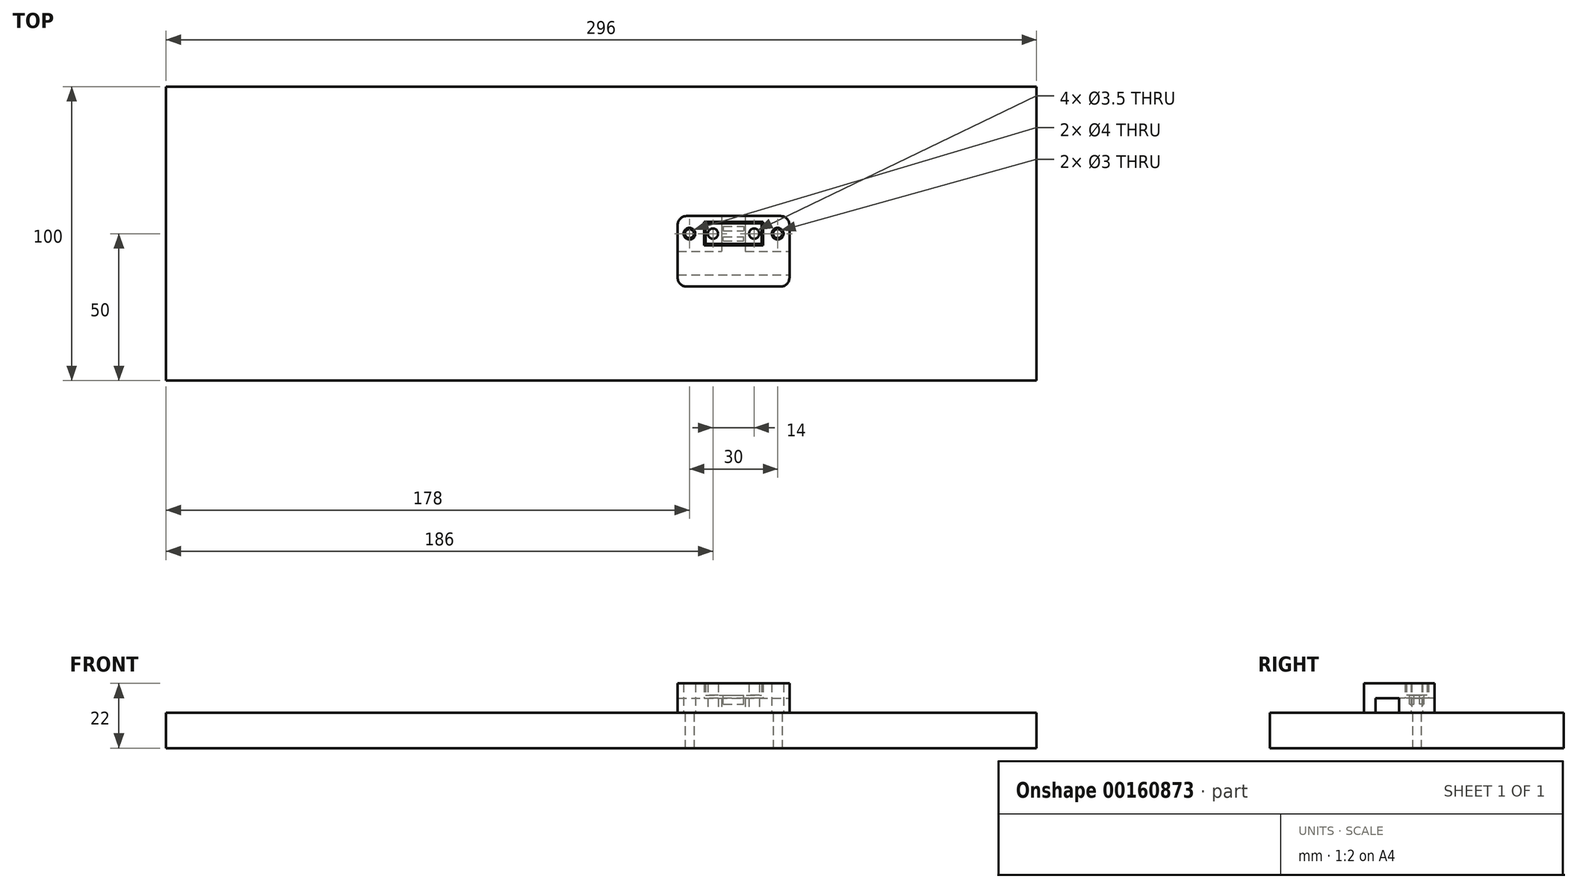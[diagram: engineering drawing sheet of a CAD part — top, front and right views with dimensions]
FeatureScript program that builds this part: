
annotation { "Feature Type Name" : "Feature", "Feature Type Description" : "" }
export const myFeature = defineFeature(function(context is Context, id is Id, definition is map)
    precondition{}
    {
        {
            var Q0;
            Q0=qCreatedBy(makeId("Top.planeOp"),FACE);
            var sketch = newSketch(context, id + "F0", { "sketchPlane" : qUnion([Q0])});
            skLineSegment(sketch, "E0.bottom", {"start": v(-148, 50) * mm, "end": v(148, 50) * mm});
            skLineSegment(sketch, "E0.top", {"start": v(-148, -50) * mm, "end": v(148, -50) * mm});
            skLineSegment(sketch, "E0.left", {"start": v(-148, 50) * mm, "end": v(-148, -50) * mm});
            skLineSegment(sketch, "E0.right", {"start": v(148, 50) * mm, "end": v(148, -50) * mm});
            skPoint(sketch, "E1", {"position": v(0, 50) * mm});
            skPoint(sketch, "E2", {"position": v(148, 0) * mm});
            skCircle(sketch, "E3", {"center": v(60, 0) * mm, "radius": 1.5 * mm});
            skCircle(sketch, "E4.MirrorC", {"center": v(30, 0) * mm, "radius": 1.5 * mm});
            skSolve(sketch);
        }
        {
            var Q0;
            Q0 = qSketchRegion(id + "F0", true);
            extrude(context, id + "F1", {"entities" : qUnion([Q0]), "depth" : 12 * mm});
        }
        {
            var Q0;
            Q0=makeQuery(id+"F1.opExtrude","CAP_FACE",FACE,{"disambiguationData":[OSD([sQuery(id+"F0.wireOp",EDGE,"E0.bottom"),sQuery(id+"F0.wireOp",EDGE,"E0.top"),sQuery(id+"F0.wireOp",EDGE,"E0.left"),sQuery(id+"F0.wireOp",EDGE,"E0.right"),sQuery(id+"F0.wireOp",EDGE,"E3"),sQuery(id+"F0.wireOp",EDGE,"E4.MirrorC")])],"isStart":false});
            var sketch = newSketch(context, id + "F2", { "sketchPlane" : qUnion([Q0])});
            skLineSegment(sketch, "E5", {"start": v(30, 0) * mm, "end": v(60, 0) * mm, "construction": true});
            skLineSegment(sketch, "E6", {"start": v(45, 0) * mm, "end": v(45, 6) * mm, "construction": true});
            skLineSegment(sketch, "E7", {"start": v(29, 6) * mm, "end": v(41, 6) * mm});
            skLineSegment(sketch, "E8.MirrorCS", {"start": v(29, -18) * mm, "end": v(61, -18) * mm});
            skArc(sketch, "E9", {"start": v(64, 3) * mm, "mid": v(63.12, 5.12) * mm, "end": v(61, 6) * mm});
            skArc(sketch, "E10.MirrorCS", {"start": v(26, 3) * mm, "mid": v(26.88, 5.12) * mm, "end": v(29, 6) * mm});
            skArc(sketch, "E11", {"start": v(61, -18) * mm, "mid": v(63.12, -17.12) * mm, "end": v(64, -15) * mm});
            skLineSegment(sketch, "E12", {"start": v(64, -15) * mm, "end": v(64, -14) * mm});
            skArc(sketch, "E13.MirrorCS", {"start": v(29, -18) * mm, "mid": v(26.88, -17.12) * mm, "end": v(26, -15) * mm});
            skLineSegment(sketch, "E14.MirrorCS", {"start": v(26, -15) * mm, "end": v(26, -14) * mm});
            skLineSegment(sketch, "E15", {"start": v(26, -14) * mm, "end": v(64, -14) * mm});
            skLineSegment(sketch, "E16", {"start": v(26, -6) * mm, "end": v(41, -6) * mm});
            skLineSegment(sketch, "E17.trimOffspring", {"start": v(26, -6) * mm, "end": v(26, 3) * mm});
            skLineSegment(sketch, "E18.trimOffspring", {"start": v(64, -6) * mm, "end": v(64, 3) * mm});
            skLineSegment(sketch, "E19", {"start": v(41, 6) * mm, "end": v(41, -6) * mm});
            skLineSegment(sketch, "E20.MirrorCS", {"start": v(49, 6) * mm, "end": v(49, -6) * mm});
            skLineSegment(sketch, "E21.trimOffspring", {"start": v(49, 6) * mm, "end": v(61, 6) * mm});
            skLineSegment(sketch, "E22.trimOffspring", {"start": v(49, -6) * mm, "end": v(64, -6) * mm});
            skCircle(sketch, "E23", {"center": v(60, 0) * mm, "radius": 2 * mm});
            skCircle(sketch, "E24.MirrorC", {"center": v(30, 0) * mm, "radius": 2 * mm});
            skCircle(sketch, "E25", {"center": v(38, 0) * mm, "radius": 1.75 * mm});
            skCircle(sketch, "E26.MirrorC", {"center": v(52, 0) * mm, "radius": 1.75 * mm});
            skSolve(sketch);
        }
        {
            var Q0;
            Q0 = qSketchRegion(id + "F2", true);
            extrude(context, id + "F3", {"entities" : qUnion([Q0]), "depth" : 5 * mm});
        }
        {
            var Q0;
            Q0=makeQuery(id+"F3.opExtrude","CAP_FACE",FACE,{"disambiguationData":[OSD([sQuery(id+"F2.wireOp",EDGE,"E8.MirrorCS"),sQuery(id+"F2.wireOp",EDGE,"E11"),sQuery(id+"F2.wireOp",EDGE,"E12"),sQuery(id+"F2.wireOp",EDGE,"E13.MirrorCS"),sQuery(id+"F2.wireOp",EDGE,"E14.MirrorCS"),sQuery(id+"F2.wireOp",EDGE,"E15")])],"isStart":false});
            var sketch = newSketch(context, id + "F4", { "sketchPlane" : qUnion([Q0])});
            skArc(sketch, "E27", {"start": v(61, -18) * mm, "mid": v(63.12, -17.12) * mm, "end": v(64, -15) * mm});
            skLineSegment(sketch, "E28", {"start": v(64, -15) * mm, "end": v(64, 3) * mm});
            skLineSegment(sketch, "E29", {"start": v(45, -14) * mm, "end": v(45, -6) * mm, "construction": true});
            skLineSegment(sketch, "E30", {"start": v(64, -6) * mm, "end": v(45, -6) * mm, "construction": true});
            skArc(sketch, "E31.MirrorCS", {"start": v(61, 6) * mm, "mid": v(63.12, 5.12) * mm, "end": v(64, 3) * mm});
            skArc(sketch, "E32.MirrorCS", {"start": v(29, -18) * mm, "mid": v(26.88, -17.12) * mm, "end": v(26, -15) * mm});
            skLineSegment(sketch, "E33.MirrorCS", {"start": v(26, -15) * mm, "end": v(26, 3) * mm});
            skArc(sketch, "E34.MirrorCS", {"start": v(29, 6) * mm, "mid": v(26.88, 5.12) * mm, "end": v(26, 3) * mm});
            skLineSegment(sketch, "E35", {"start": v(29, -18) * mm, "end": v(61, -18) * mm});
            skLineSegment(sketch, "E36", {"start": v(61, 6) * mm, "end": v(29, 6) * mm});
            skLineSegment(sketch, "E37", {"start": v(35, 4) * mm, "end": v(55, 4) * mm});
            skLineSegment(sketch, "E38", {"start": v(55, 4) * mm, "end": v(55, -4) * mm});
            skLineSegment(sketch, "E39", {"start": v(55, -4) * mm, "end": v(35, -4) * mm});
            skLineSegment(sketch, "E40.MirrorCS", {"start": v(35, 4) * mm, "end": v(35, -4) * mm});
            skCircle(sketch, "E41", {"center": v(60, 0) * mm, "radius": 2 * mm});
            skCircle(sketch, "E42.MirrorC", {"center": v(30, 0) * mm, "radius": 2 * mm});
            skSolve(sketch);
        }
        {
            var Q0;
            Q0 = qSketchRegion(id + "F4", true);
            extrude(context, id + "F5", {"entities" : qUnion([Q0]), "operationType" : NewBodyOperationType.ADD, "depth" : 5 * mm});
        }
        {
            var Q0;
            Q0=makeQuery(id+"F3.opExtrude","CAP_FACE",FACE,{"disambiguationData":[OSD([sQuery(id+"F2.wireOp",EDGE,"E9"),sQuery(id+"F2.wireOp",EDGE,"E18.trimOffspring"),sQuery(id+"F2.wireOp",EDGE,"E20.MirrorCS"),sQuery(id+"F2.wireOp",EDGE,"E21.trimOffspring"),sQuery(id+"F2.wireOp",EDGE,"E22.trimOffspring"),sQuery(id+"F2.wireOp",EDGE,"E23"),sQuery(id+"F2.wireOp",EDGE,"E26.MirrorC")])],"isStart":false});
            var sketch = newSketch(context, id + "F6", { "sketchPlane" : qUnion([Q0])});
            skLineSegment(sketch, "E43", {"start": v(35.5, 3.5) * mm, "end": v(54.5, 3.5) * mm});
            skLineSegment(sketch, "E44", {"start": v(54.5, 3.5) * mm, "end": v(54.5, -3.5) * mm});
            skLineSegment(sketch, "E45", {"start": v(54.5, -3.5) * mm, "end": v(35.5, -3.5) * mm});
            skLineSegment(sketch, "E46", {"start": v(45, -4) * mm, "end": v(45, 4) * mm, "construction": true});
            skLineSegment(sketch, "E47.MirrorCS", {"start": v(35.5, 3.5) * mm, "end": v(35.5, -3.5) * mm});
            skCircle(sketch, "E48", {"center": v(52, 0) * mm, "radius": 1.75 * mm});
            skCircle(sketch, "E49.MirrorC", {"center": v(38, 0) * mm, "radius": 1.75 * mm});
            skSolve(sketch);
        }
        {
            var Q0;
            Q0 = qSketchRegion(id + "F6", true);
            extrude(context, id + "F7", {"entities" : qUnion([Q0]), "depth" : 5 * mm, "hasSecondDirection" : true, "secondDirectionOppositeDirection" : false, "secondDirectionDepth" : 1 * mm});
        }
        {
            var Q0;
            Q0=makeQuery(id+"F7.opExtrude","CAP_FACE",FACE,{"disambiguationData":[OSD([sQuery(id+"F6.wireOp",EDGE,"E43"),sQuery(id+"F6.wireOp",EDGE,"E44"),sQuery(id+"F6.wireOp",EDGE,"E45"),sQuery(id+"F6.wireOp",EDGE,"E47.MirrorCS")])],"isStart":true});
            var sketch = newSketch(context, id + "F8", { "sketchPlane" : qUnion([Q0])});
            skLineSegment(sketch, "E50.bottom", {"start": v(41.5, 2.5) * mm, "end": v(48.5, 2.5) * mm});
            skLineSegment(sketch, "E50.top", {"start": v(41.5, 1) * mm, "end": v(48.5, 1) * mm});
            skLineSegment(sketch, "E50.right", {"start": v(48.5, 2.5) * mm, "end": v(48.5, 1) * mm});
            skLineSegment(sketch, "E51", {"start": v(45, -3.5) * mm, "end": v(45, 3.5) * mm, "construction": true});
            skLineSegment(sketch, "E52.MirrorCS", {"start": v(41.5, 2.5) * mm, "end": v(41.5, 1) * mm});
            skLineSegment(sketch, "E53.MirrorCS", {"start": v(41.5, -1) * mm, "end": v(48.5, -1) * mm});
            skLineSegment(sketch, "E54.MirrorCS", {"start": v(48.5, -2.5) * mm, "end": v(48.5, -1) * mm});
            skLineSegment(sketch, "E55.MirrorCS", {"start": v(41.5, -2.5) * mm, "end": v(48.5, -2.5) * mm});
            skLineSegment(sketch, "E56.MirrorCS", {"start": v(41.5, -2.5) * mm, "end": v(41.5, -1) * mm});
            skSolve(sketch);
        }
        {
            var Q0;
            Q0 = qSketchRegion(id + "F8", true);
            extrude(context, id + "F9", {"entities" : qUnion([Q0]), "operationType" : NewBodyOperationType.ADD, "depth" : 3 * mm});
        }
    });
